# Revit family: Network IO Expander-Audio-Q-SYS-QIO-AES8x8
name_source: partatom
category: Communication Devices
units: mm (PartAtom-declared; Revit-internal decimal feet)

## family parameters
Cut with Voids When Loaded = No
Host = Face
Maintain Annotation Orientation = No
OmniClass Number = 23.85.10.17.11
OmniClass Title = Audio-Visual System Components
Part Type = Normal
Room Calculation Point = No
Round Connector Dimension = Use Diameter
Shared = No

## types (1)
- AES8x8
    Apparent Load = 67 VA
    Body Material = Paint - Q-SYS - Black
    Body Offset = 0 "
    Body Width = 4.3 "
    Default Elevation = 48 "
    Depth = 8.5 "
    Description = Surface mounted network IO expander for Q-SYS platform.
    Frame Depth = 0.1 "
    Grille Material = Paint - Q-SYS - Black Mesh 2
    Height = 1.7 "
    Highlight Material = Plastic - Q-SYS - Black
    IQ Category = Network IO Expander
    LED Material = Plastic - Q-SYS - LED Blue
    Length 1 = 0.1 "
    Load Classification = Other
    Manufacturer = Q-SYS
    Manufacturer URL = https://www.qsys.com
    Minimum Circuit Amps = 3 A
    Model = AES8x8
    Number of Poles = 2
    Power Factor = 0.9
    Product Documentation Link = https://www.qsys.com
    Product Page URL = https://www.qsys.com
    Type Comments = AES8x8
    URL = https://www.qsys.com
    Voltage = 24 V
    Weight = 1.72 lbm
    Weight Dimensional = 1.72
    Weight Product = 1.72
    Width = 4.3 "

## geometry (parser evidence)
native form markers: Sweep x2
no freeform markers — native parametric forms only
